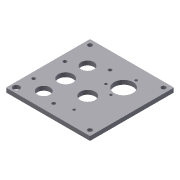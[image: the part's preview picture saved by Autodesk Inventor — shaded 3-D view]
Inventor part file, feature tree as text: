
AUTODESK INVENTOR PART (.ipt)
format: ipt  version: 2011 (Build 150239000, 239)  size: 143,360 bytes
history: native  units: in
note: dims shown in document units (in); Inventor stores cm internally (conversion verified against a paired STEP export)
features: other x1, imported_body x1, extrude x1, sketch x1
ambient origin geometry x8: Origin, YZ Plane, XZ Plane, XY Plane, X Axis, Y Axis, Z Axis, Center Point
feature tree (4):
  other  "super_d04"
  imported_body  "Base1"
  extrude  "Extrusion1"  Depth=0.0312in TaperAngle=0.0deg
  sketch  "Sketch1"  dims[d0=0.51in d1=0.0312in d2=0.0in]
